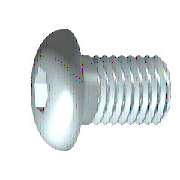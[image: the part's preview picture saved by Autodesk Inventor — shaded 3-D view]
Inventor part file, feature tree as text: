
AUTODESK INVENTOR PART (.ipt)
format: ipt  version: 2024.1 (Build 281209000, 209)  size: 184,832 bytes
history: native  units: mm (DEFAULTED — no unit token found)
features: extrude x1, plane x1, fillet x1
ambient origin geometry x7: Origin, YZ Plane, XY Plane, X Axis, Y Axis, Z Axis, Center Point
bodies: Solid1 (feature_tree), Body (feature_tree)
feature tree (3):
  extrude  "Slot"  Depth=18.0mm
  plane  "Work Plane1"
  fillet  "Fillet2"  Radius=0.306825mm
